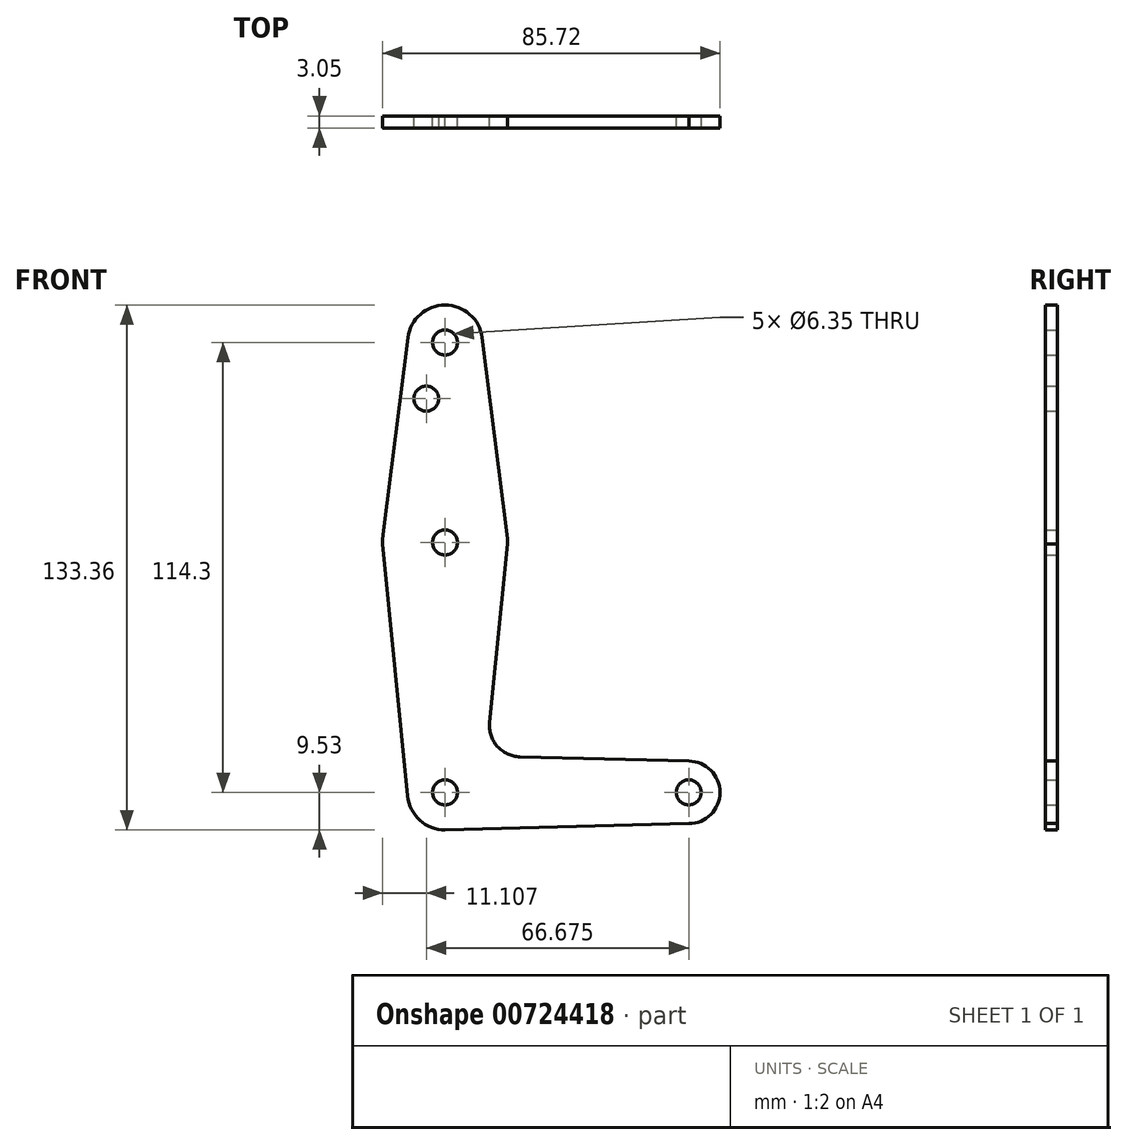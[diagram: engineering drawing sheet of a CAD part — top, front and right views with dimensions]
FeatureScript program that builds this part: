
annotation { "Feature Type Name" : "Feature", "Feature Type Description" : "" }
export const myFeature = defineFeature(function(context is Context, id is Id, definition is map)
    precondition{}
    {
        {
            var Q0;
            Q0=qCreatedBy(makeId("Front.planeOp"),FACE);
            var sketch = newSketch(context, id + "F0", { "sketchPlane" : qUnion([Q0])});
            skLineSegment(sketch, "E0", {"start": v(0, 114.3) * mm, "end": v(0, 0) * mm, "construction": true});
            skLineSegment(sketch, "E1", {"start": v(0, 0) * mm, "end": v(61.91, 0) * mm, "construction": true});
            skCircle(sketch, "E2", {"center": v(0, 114.3) * mm, "radius": 9.53 * mm});
            skCircle(sketch, "E3", {"center": v(0, 63.5) * mm, "radius": 15.88 * mm});
            skCircle(sketch, "E4", {"center": v(0, 0) * mm, "radius": 9.53 * mm});
            skCircle(sketch, "E5", {"center": v(61.91, 0) * mm, "radius": 7.94 * mm});
            skLineSegment(sketch, "E6", {"start": v(-9.44, 115.55) * mm, "end": v(-15.75, 65.48) * mm});
            skLineSegment(sketch, "E7", {"start": v(9.44, 115.55) * mm, "end": v(15.75, 65.48) * mm});
            skLineSegment(sketch, "E8", {"start": v(-15.87, 63.15) * mm, "end": v(-9.48, -0.95) * mm});
            skLineSegment(sketch, "E9", {"start": v(11.31, 17.78) * mm, "end": v(15.87, 63.15) * mm});
            skLineSegment(sketch, "E10", {"start": v(19.02, 9.04) * mm, "end": v(61.91, 7.94) * mm});
            skLineSegment(sketch, "E11", {"start": v(0, -9.52) * mm, "end": v(61.91, -7.94) * mm});
            skCircle(sketch, "E12", {"center": v(0, 114.3) * mm, "radius": 3.18 * mm});
            skCircle(sketch, "E13", {"center": v(0, 63.5) * mm, "radius": 3.18 * mm});
            skCircle(sketch, "E14", {"center": v(-4.76, 100.03) * mm, "radius": 3.18 * mm});
            skCircle(sketch, "E15", {"center": v(0, 0) * mm, "radius": 3.18 * mm});
            skCircle(sketch, "E16", {"center": v(61.91, 0) * mm, "radius": 3.18 * mm});
            skPoint(sketch, "E17.newPointB", {"position": v(0, 9.52) * mm});
            skArc(sketch, "E17.filletArc", {"start": v(11.31, 17.78) * mm, "mid": v(13.26, 11.73) * mm, "end": v(19.02, 9.04) * mm});
            skSolve(sketch);
        }
        {
            var Q0;
            {var subQ1=sQuery(id+"F0.wireOp",EDGE,"E6");Q0=makeQuery(id+"F0.imprint","IMPRINT",FACE,{"disambiguationData":[TD([[makeQuery(id+"F0.imprint","IMPRINT",EDGE,{"derivedFrom":subQ1}),1.0]])]});}
            var Q1;
            Q1=makeQuery(id+"F0.imprint","IMPRINT",FACE,{"disambiguationData":[TD([[makeQuery(id+"F0.imprint","IMPRINT",EDGE,{"derivedFrom":sQuery(id+"F0.wireOp",EDGE,"E13")}),-1.0]])]});
            var Q2;
            {var subQ8=sQuery(id+"F0.wireOp",EDGE,"E10");Q2=makeQuery(id+"F0.imprint","IMPRINT",FACE,{"disambiguationData":[TD([[makeQuery(id+"F0.imprint","IMPRINT",EDGE,{"derivedFrom":subQ8}),-1.0]])]});}
            var Q3;
            Q3=makeQuery(id+"F0.imprint","IMPRINT",FACE,{"disambiguationData":[TD([[makeQuery(id+"F0.imprint","IMPRINT",EDGE,{"derivedFrom":sQuery(id+"F0.wireOp",EDGE,"E15")}),-1.0]])]});
            var Q4;
            Q4=makeQuery(id+"F0.imprint","IMPRINT",FACE,{"disambiguationData":[TD([[makeQuery(id+"F0.imprint","IMPRINT",EDGE,{"derivedFrom":sQuery(id+"F0.wireOp",EDGE,"E16")}),-1.0]])]});
            var Q5;
            Q5=makeQuery(id+"F0.imprint","IMPRINT",FACE,{"disambiguationData":[TD([[makeQuery(id+"F0.imprint","IMPRINT",EDGE,{"derivedFrom":sQuery(id+"F0.wireOp",EDGE,"E12")}),-1.0]])]});
            extrude(context, id + "F1", {"entities" : qUnion([Q0, Q1, Q2, Q3, Q4, Q5]), "depth" : 3.05 * mm, "offsetDistance" : 25.4 * mm});
        }
    });
